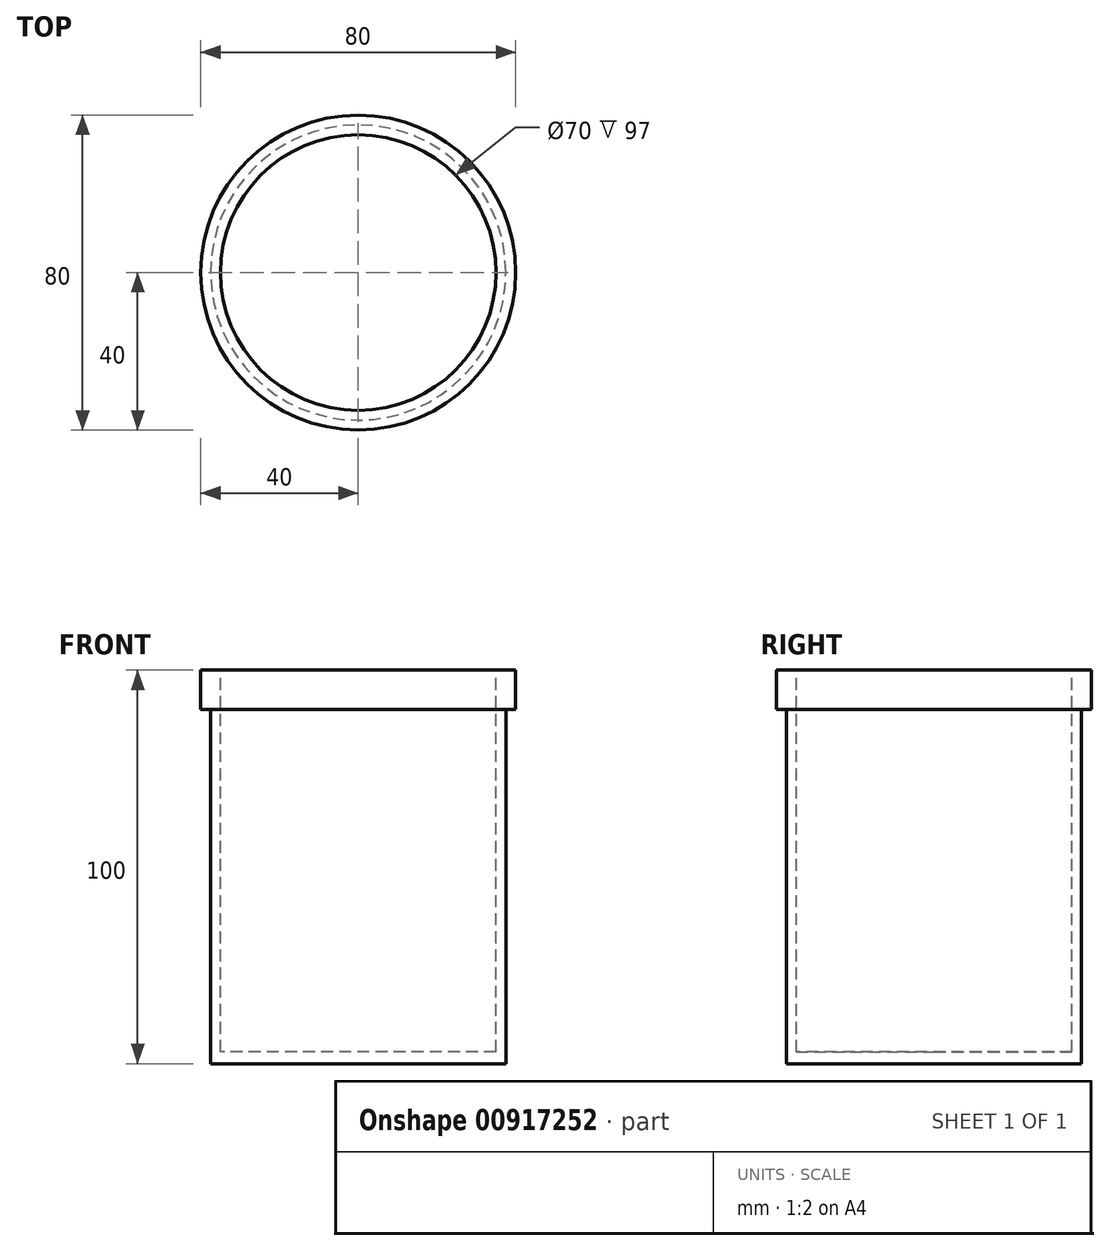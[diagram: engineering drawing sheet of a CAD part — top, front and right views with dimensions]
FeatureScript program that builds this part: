
annotation { "Feature Type Name" : "Feature", "Feature Type Description" : "" }
export const myFeature = defineFeature(function(context is Context, id is Id, definition is map)
    precondition{}
    {
        {
            var Q0;
            Q0=qCreatedBy(makeId("Front.planeOp"),FACE);
            var sketch = newSketch(context, id + "F0", { "sketchPlane" : qUnion([Q0])});
            skLineSegment(sketch, "E0", {"start": v(0, 50) * mm, "end": v(0, -50) * mm, "construction": true});
            skLineSegment(sketch, "E1", {"start": v(0, 50) * mm, "end": v(35, 50) * mm, "construction": true});
            skLineSegment(sketch, "E2", {"start": v(35, 50) * mm, "end": v(35, -47) * mm});
            skLineSegment(sketch, "E3", {"start": v(35, -47) * mm, "end": v(0, -47) * mm});
            skLineSegment(sketch, "E4", {"start": v(0, -47) * mm, "end": v(0, -50) * mm});
            skLineSegment(sketch, "E5", {"start": v(0, -50) * mm, "end": v(37.5, -50) * mm});
            skLineSegment(sketch, "E6", {"start": v(37.5, -50) * mm, "end": v(37.5, 40) * mm});
            skLineSegment(sketch, "E7", {"start": v(37.5, 40) * mm, "end": v(40, 40) * mm});
            skLineSegment(sketch, "E8", {"start": v(40, 40) * mm, "end": v(40, 50) * mm});
            skLineSegment(sketch, "E9", {"start": v(40, 50) * mm, "end": v(35, 50) * mm});
            skSolve(sketch);
        }
        {
            var Q0;
            Q0 = qSketchRegion(id + "F0", true);
            var Q1;
            Q1=sQuery(id+"F0.wireOp",EDGE,"E0");
            revolve(context, id + "F1", {"surfaceOperationType" : NewSurfaceOperationType.NEW, "entities" : qUnion([Q0]), "axis" : qUnion([Q1]), "revolveType" : RevolveType.FULL});
        }
    });
